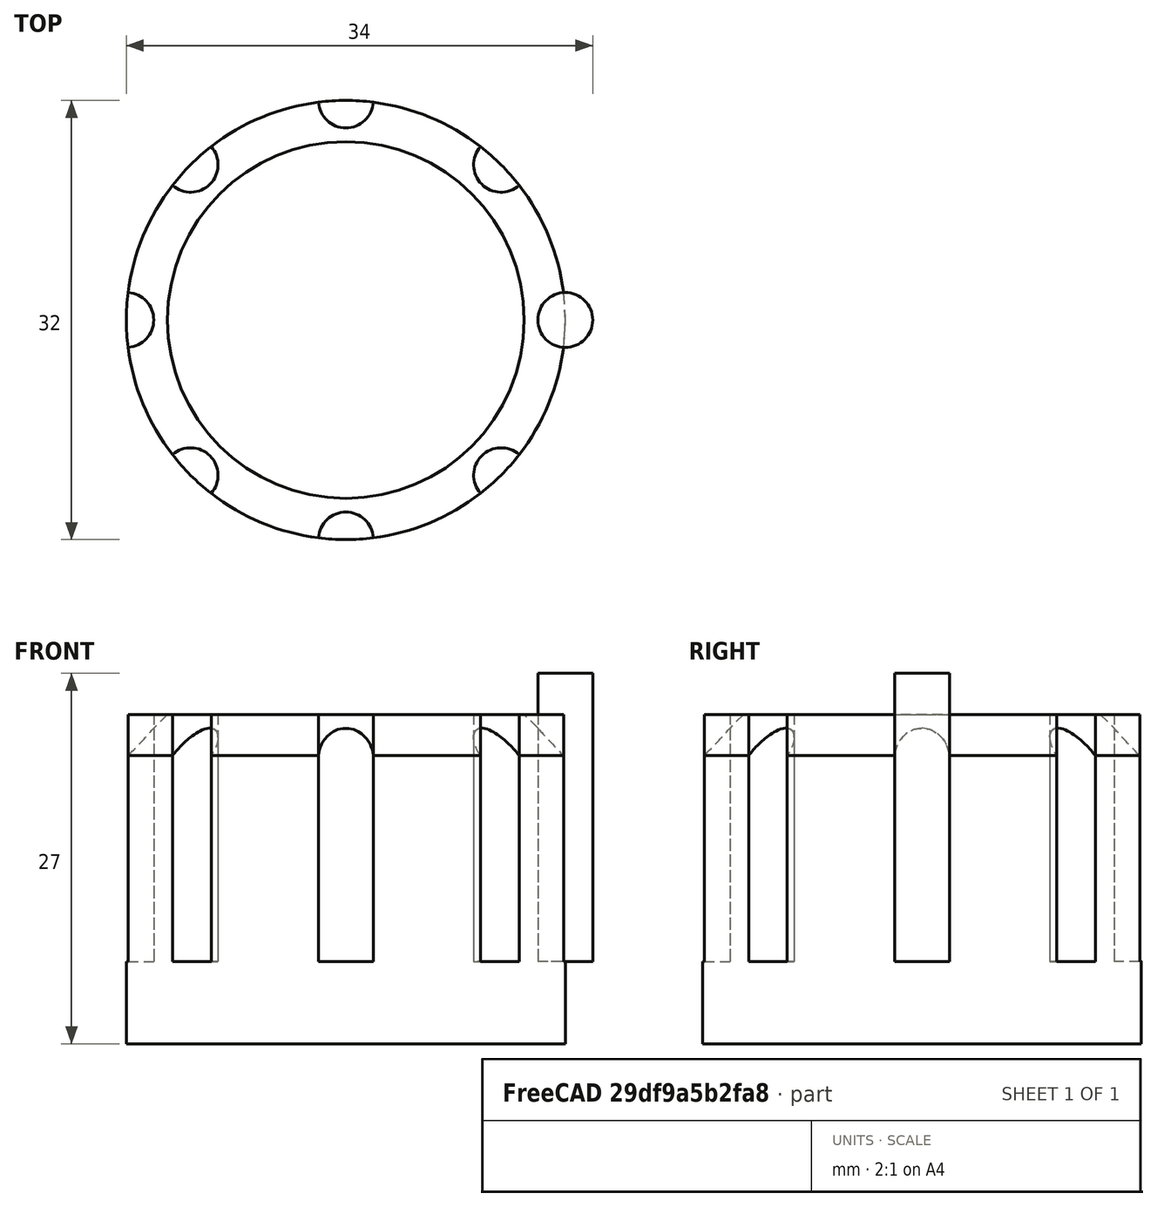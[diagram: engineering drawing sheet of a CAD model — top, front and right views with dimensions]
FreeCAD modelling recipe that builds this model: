
FCSTD DOCUMENT  (FreeCAD 1.0R39285 (Git))
Label: ojt1_t12r01_buttom_potenciometer
License: All rights reserved
objects: Part::Cylinder×2, Part::Cut×2, Part::FeaturePython×1, Part::Chamfer×1
note: 5 computed .brp shape members not serialized (recipe doc carries the construction recipe); baked Part::Feature solids carry a one-line shape summary decoded from their .brp

FEATURE [Part::Cylinder] Cylinder  label="Cilindre"
  Angle = 360
  AttacherType = Attacher::AttachEngine3D
  FirstAngle = 0
  Height = 24
  Radius = 16
  SecondAngle = 0
FEATURE [Part::Cylinder] Cylinder001  label="Cilindre001"
  Angle = 360
  AttacherType = Attacher::AttachEngine3D
  FirstAngle = 0
  Height = 21
  Placement = pos=(16,0,6) rot=(0,0,1;0rad)
  Radius = 2
  SecondAngle = 0
FEATURE [Part::FeaturePython] Array  # Draft array (typed FeaturePython)
  AlwaysSyncPlacement = false
  Angle = 360
  ArrayType = 1
  Axis = (0,0,1)
  Base = -> Cylinder001
  Center = (0,0,1)
  Count = 8
  ExpandArray = false
  Fuse = false
  IntervalAxis = (0,0,0)
  IntervalX = (50,0,0)
  IntervalY = (0,50,0)
  IntervalZ = (0,0,50)
  NumberCircles = 3
  NumberPolar = 8
  NumberX = 2
  NumberY = 2
  NumberZ = 1
  PlacementList = 8 placements: [(16,0,6),(11.3137,11.3137,6),(0,16,6),(-11.3137,11.3137,6),(-16,1.95943e-15,6),(-11.3137,-11.3137,6),(-3.55271e-15,-16,6),(11.3137,-11.3137,6)]
  RadialDistance = 50
  ScaleList = (8) [(1,1,1),(1,1,1),(1,1,1),(1,1,1),(1,1,1),(1,1,1),(1,1,1),(1,1,1)]
  Symmetry = 1
  TangentialDistance = 25
FEATURE [Part::Cut] Cut
  Base = -> Cylinder
  Refine = true
  Tool = -> Array
FEATURE [Part::Chamfer] Chamfer
  Base = -> Cylinder
  EdgeLinks = -> Cylinder [Edge3]
  Edges = 1 edges r=3: [Edge3]
FEATURE [Part::Cut] Cut001
  Base = -> Chamfer
  Refine = true
  Tool = -> Array
